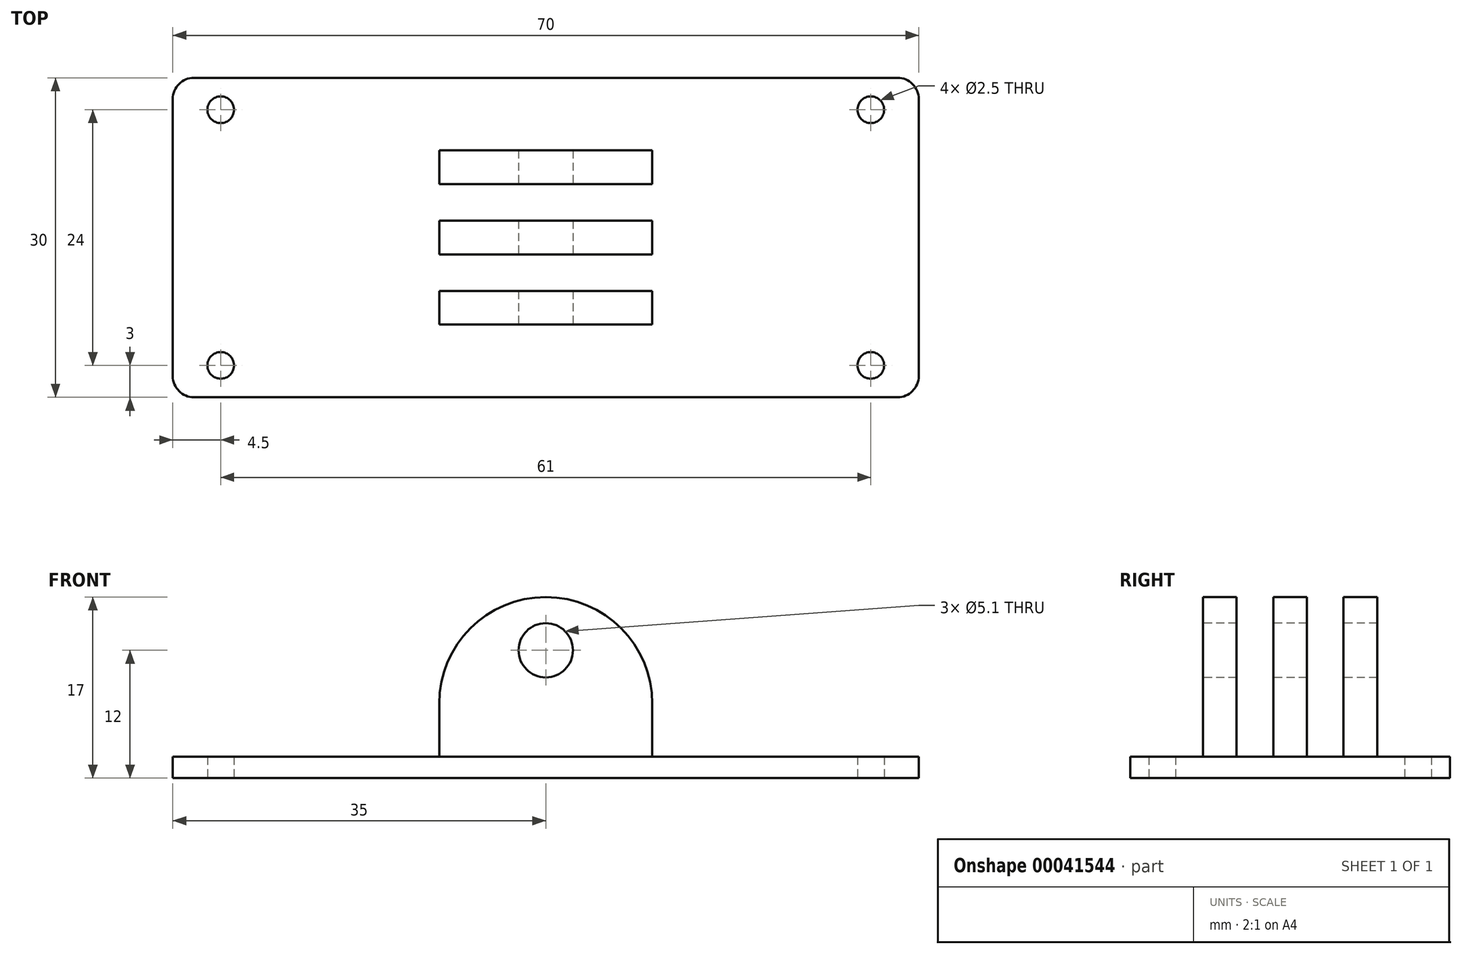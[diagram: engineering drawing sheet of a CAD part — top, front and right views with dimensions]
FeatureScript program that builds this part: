
annotation { "Feature Type Name" : "Feature", "Feature Type Description" : "" }
export const myFeature = defineFeature(function(context is Context, id is Id, definition is map)
    precondition{}
    {
        {
            var Q0;
            Q0=qCreatedBy(makeId("Top.planeOp"),FACE);
            var sketch = newSketch(context, id + "F0", { "sketchPlane" : qUnion([Q0])});
            skLineSegment(sketch, "E0.rect.bottom", {"start": v(33, -15) * mm, "end": v(-33, -15) * mm});
            skLineSegment(sketch, "E0.rect.top", {"start": v(33, 15) * mm, "end": v(-33, 15) * mm});
            skLineSegment(sketch, "E0.rect.left", {"start": v(35, -13) * mm, "end": v(35, 13) * mm});
            skLineSegment(sketch, "E0.rect.right", {"start": v(-35, -13) * mm, "end": v(-35, 13) * mm});
            skPoint(sketch, "E0.rect.middle", {"position": v(0, 0) * mm});
            skCircle(sketch, "E1", {"center": v(-30.5, 12) * mm, "radius": 1.25 * mm});
            skLineSegment(sketch, "E2", {"start": v(0, 0) * mm, "end": v(0, -15) * mm, "construction": true});
            skLineSegment(sketch, "E3", {"start": v(0, 0) * mm, "end": v(-35, 0) * mm, "construction": true});
            skCircle(sketch, "E4.0.MirrorC", {"center": v(30.5, 12) * mm, "radius": 1.25 * mm});
            skLineSegment(sketch, "E5.0.MirrorCS", {"start": v(0, 0) * mm, "end": v(35, 0) * mm, "construction": true});
            skCircle(sketch, "E6.0.MirrorC", {"center": v(-30.5, -12) * mm, "radius": 1.25 * mm});
            skCircle(sketch, "E7.0.MirrorC", {"center": v(30.5, -12) * mm, "radius": 1.25 * mm});
            skPoint(sketch, "E8.visualSharp", {"position": v(-35, 15) * mm});
            skArc(sketch, "E8.filletArc", {"start": v(-33, 15) * mm, "mid": v(-34.41, 14.41) * mm, "end": v(-35, 13) * mm});
            skPoint(sketch, "E9.visualSharp", {"position": v(-35, -15) * mm});
            skArc(sketch, "E9.filletArc", {"start": v(-35, -13) * mm, "mid": v(-34.41, -14.41) * mm, "end": v(-33, -15) * mm});
            skPoint(sketch, "E10.visualSharp", {"position": v(35, -15) * mm});
            skArc(sketch, "E10.filletArc", {"start": v(33, -15) * mm, "mid": v(34.41, -14.41) * mm, "end": v(35, -13) * mm});
            skPoint(sketch, "E11.visualSharp", {"position": v(35, 15) * mm});
            skArc(sketch, "E11.filletArc", {"start": v(35, 13) * mm, "mid": v(34.41, 14.41) * mm, "end": v(33, 15) * mm});
            skSolve(sketch);
        }
        {
            var Q0;
            Q0=qSketchRegion(id+"F0",true);
            extrude(context, id + "F1", {"entities" : qUnion([Q0]), "depth" : 2 * mm});
        }
        {
            var Q0;
            Q0=makeQuery(id+"F1.opExtrude","CAP_FACE",FACE,{"disambiguationData":[OSD([sQuery(id+"F0.wireOp",EDGE,"E0.rect.bottom"),sQuery(id+"F0.wireOp",EDGE,"E0.rect.top"),sQuery(id+"F0.wireOp",EDGE,"E0.rect.left"),sQuery(id+"F0.wireOp",EDGE,"E0.rect.right"),sQuery(id+"F0.wireOp",EDGE,"E1"),sQuery(id+"F0.wireOp",EDGE,"E4.0.MirrorC"),sQuery(id+"F0.wireOp",EDGE,"E6.0.MirrorC"),sQuery(id+"F0.wireOp",EDGE,"E7.0.MirrorC"),sQuery(id+"F0.wireOp",EDGE,"E8.filletArc"),sQuery(id+"F0.wireOp",EDGE,"E9.filletArc"),sQuery(id+"F0.wireOp",EDGE,"E10.filletArc"),sQuery(id+"F0.wireOp",EDGE,"E11.filletArc")])],"isStart":false});
            var sketch = newSketch(context, id + "F2", { "sketchPlane" : qUnion([Q0])});
            skLineSegment(sketch, "E12.rect.bottom", {"start": v(10, -1.58) * mm, "end": v(-10, -1.58) * mm});
            skLineSegment(sketch, "E12.rect.top", {"start": v(10, 1.57) * mm, "end": v(-10, 1.57) * mm});
            skLineSegment(sketch, "E12.rect.left", {"start": v(10, -1.58) * mm, "end": v(10, 1.57) * mm});
            skLineSegment(sketch, "E12.rect.right", {"start": v(-10, -1.58) * mm, "end": v(-10, 1.57) * mm});
            skPoint(sketch, "E12.rect.middle", {"position": v(0, 0) * mm});
            skLineSegment(sketch, "E13.0.1.0", {"start": v(-10, 5.02) * mm, "end": v(-10, 8.17) * mm});
            skLineSegment(sketch, "E13.0.1.1", {"start": v(10, 5.02) * mm, "end": v(10, 8.18) * mm});
            skLineSegment(sketch, "E13.0.1.2", {"start": v(10, 8.18) * mm, "end": v(-10, 8.18) * mm});
            skLineSegment(sketch, "E13.0.1.3", {"start": v(10, 5.02) * mm, "end": v(-10, 5.02) * mm});
            skPoint(sketch, "E13.0.1.4", {"position": v(0, 6.6) * mm});
            skLineSegment(sketch, "E13.direction1", {"start": v(-10, -1.58) * mm, "end": v(15, -1.58) * mm, "construction": true});
            skLineSegment(sketch, "E13.direction2", {"start": v(-10, -1.58) * mm, "end": v(-10, 5.02) * mm, "construction": true});
            skLineSegment(sketch, "E14.MirrorCS", {"start": v(-10, -5.02) * mm, "end": v(-10, -8.17) * mm});
            skLineSegment(sketch, "E15.MirrorCS", {"start": v(10, -8.18) * mm, "end": v(-10, -8.18) * mm});
            skLineSegment(sketch, "E16.MirrorCS", {"start": v(10, -5.02) * mm, "end": v(10, -8.18) * mm});
            skLineSegment(sketch, "E17.MirrorCS", {"start": v(10, -5.02) * mm, "end": v(-10, -5.02) * mm});
            skSolve(sketch);
        }
        {
            var Q0;
            Q0 = qSketchRegion(id + "F2", true);
            extrude(context, id + "F3", {"entities" : qUnion([Q0]), "operationType" : NewBodyOperationType.ADD, "depth" : 15 * mm});
        }
        {
            var Q0;
            Q0=makeQuery(id+"F3.opExtrude","CAP_EDGE",EDGE,{"disambiguationData":[OSD([sQuery(id+"F2.wireOp",EDGE,"E14.MirrorCS")])],"isStart":false});
            var Q1;
            Q1=makeQuery(id+"F3.opExtrude","CAP_EDGE",EDGE,{"disambiguationData":[OSD([sQuery(id+"F2.wireOp",EDGE,"E16.MirrorCS")])],"isStart":false});
            var Q2;
            Q2=makeQuery(id+"F3.opExtrude","CAP_EDGE",EDGE,{"disambiguationData":[OSD([sQuery(id+"F2.wireOp",EDGE,"E12.rect.left")])],"isStart":false});
            var Q3;
            Q3=makeQuery(id+"F3.opExtrude","CAP_EDGE",EDGE,{"disambiguationData":[OSD([sQuery(id+"F2.wireOp",EDGE,"E12.rect.right")])],"isStart":false});
            var Q4;
            Q4=makeQuery(id+"F3.opExtrude","CAP_EDGE",EDGE,{"disambiguationData":[OSD([sQuery(id+"F2.wireOp",EDGE,"E13.0.1.0")])],"isStart":false});
            var Q5;
            Q5=makeQuery(id+"F3.opExtrude","CAP_EDGE",EDGE,{"disambiguationData":[OSD([sQuery(id+"F2.wireOp",EDGE,"E13.0.1.1")])],"isStart":false});
            fillet(context, id + "F4", {"entities" : qUnion([Q0, Q1, Q2, Q3, Q4, Q5]), "radius" : 10 * mm, "tangentPropagation" : true, "allowEdgeOverflow" : false});
        }
        {
            var Q0;
            Q0=makeQuery(id+"F3.opExtrude","SWEPT_FACE",FACE,{"disambiguationData":[OSD([sQuery(id+"F2.wireOp",EDGE,"E15.MirrorCS")])]});
            var sketch = newSketch(context, id + "F5", { "sketchPlane" : qUnion([Q0])});
            skCircle(sketch, "E18", {"center": v(0, 12) * mm, "radius": 2.55 * mm});
            skSolve(sketch);
        }
        {
            var Q0;
            Q0 = qSketchRegion(id + "F5", true);
            extrude(context, id + "F6", {"entities" : qUnion([Q0]), "operationType" : NewBodyOperationType.REMOVE, "oppositeDirection" : true, "depth" : 25 * mm});
        }
    });
